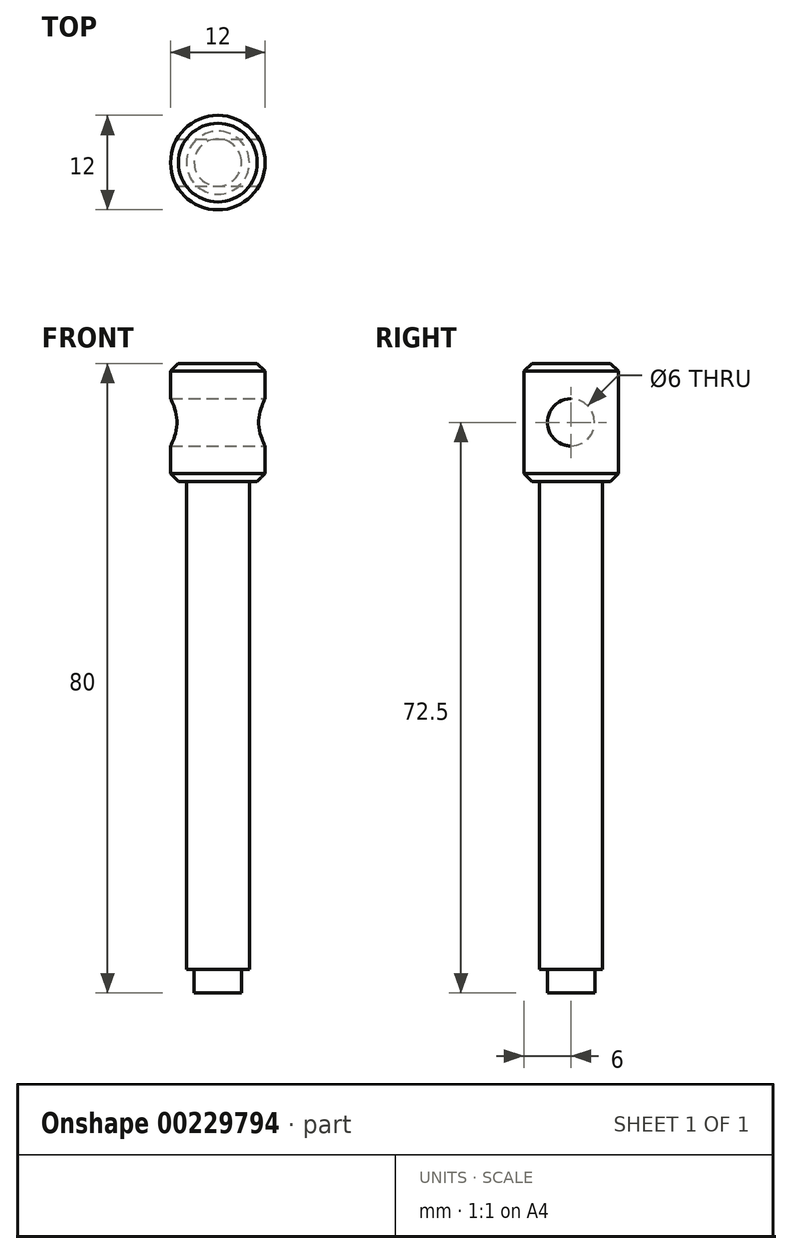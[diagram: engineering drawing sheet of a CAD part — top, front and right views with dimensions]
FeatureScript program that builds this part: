
annotation { "Feature Type Name" : "Feature", "Feature Type Description" : "" }
export const myFeature = defineFeature(function(context is Context, id is Id, definition is map)
    precondition{}
    {
        {
            var Q0;
            Q0=qCreatedBy(makeId("Front.planeOp"),FACE);
            var sketch = newSketch(context, id + "F0", { "sketchPlane" : qUnion([Q0])});
            skLineSegment(sketch, "E0", {"start": v(-4, 3) * mm, "end": v(-4, 65) * mm});
            skLineSegment(sketch, "E1", {"start": v(-4, 65) * mm, "end": v(-6, 65) * mm});
            skLineSegment(sketch, "E2", {"start": v(-6, 65) * mm, "end": v(-6, 80) * mm});
            skLineSegment(sketch, "E3", {"start": v(-6, 80) * mm, "end": v(0, 80) * mm});
            skLineSegment(sketch, "E4", {"start": v(-4, 3) * mm, "end": v(-3, 3) * mm});
            skLineSegment(sketch, "E5", {"start": v(-3, 3) * mm, "end": v(-3, 0) * mm});
            skLineSegment(sketch, "E6", {"start": v(-3, 0) * mm, "end": v(0, 0) * mm});
            skLineSegment(sketch, "E7", {"start": v(0, 80) * mm, "end": v(0, 0) * mm});
            skSolve(sketch);
        }
        {
            var Q0;
            Q0 = qSketchRegion(id + "F0", true);
            var Q1;
            Q1=sQuery(id+"F0.wireOp",EDGE,"E7");
            revolve(context, id + "F1", {"entities" : qUnion([Q0]), "axis" : qUnion([Q1]), "revolveType" : RevolveType.FULL});
        }
        {
            var Q0;
            Q0=makeQuery(id+"F1.opRevolve","SWEPT_EDGE",EDGE,{"disambiguationData":[OSD([sQuery(id+"F0.wireOp",EDGE,"E2"),sQuery(id+"F0.wireOp",EDGE,"E3")])]});
            var Q1;
            Q1=makeQuery(id+"F1.opRevolve","SWEPT_EDGE",EDGE,{"disambiguationData":[OSD([sQuery(id+"F0.wireOp",EDGE,"E1"),sQuery(id+"F0.wireOp",EDGE,"E2")])]});
            chamfer(context, id + "F2", {"entities" : qUnion([Q0, Q1]), "chamferType" : ChamferType.OFFSET_ANGLE, "width" : 1 * mm, "oppositeDirection" : false, "angle" : 45 * degree, "tangentPropagation" : true});
        }
        {
            var Q0;
            Q0=qCreatedBy(makeId("Right.planeOp"),FACE);
            var sketch = newSketch(context, id + "F3", { "sketchPlane" : qUnion([Q0])});
            skCircle(sketch, "E8", {"center": v(0, 72.5) * mm, "radius": 3 * mm});
            skSolve(sketch);
        }
        {
            var Q0;
            Q0 = qSketchRegion(id + "F3", true);
            extrude(context, id + "F4", {"entities" : qUnion([Q0]), "operationType" : NewBodyOperationType.REMOVE, "endBound" : BoundingType.SYMMETRIC, "oppositeDirection" : true, "depth" : 25 * mm});
        }
    });
